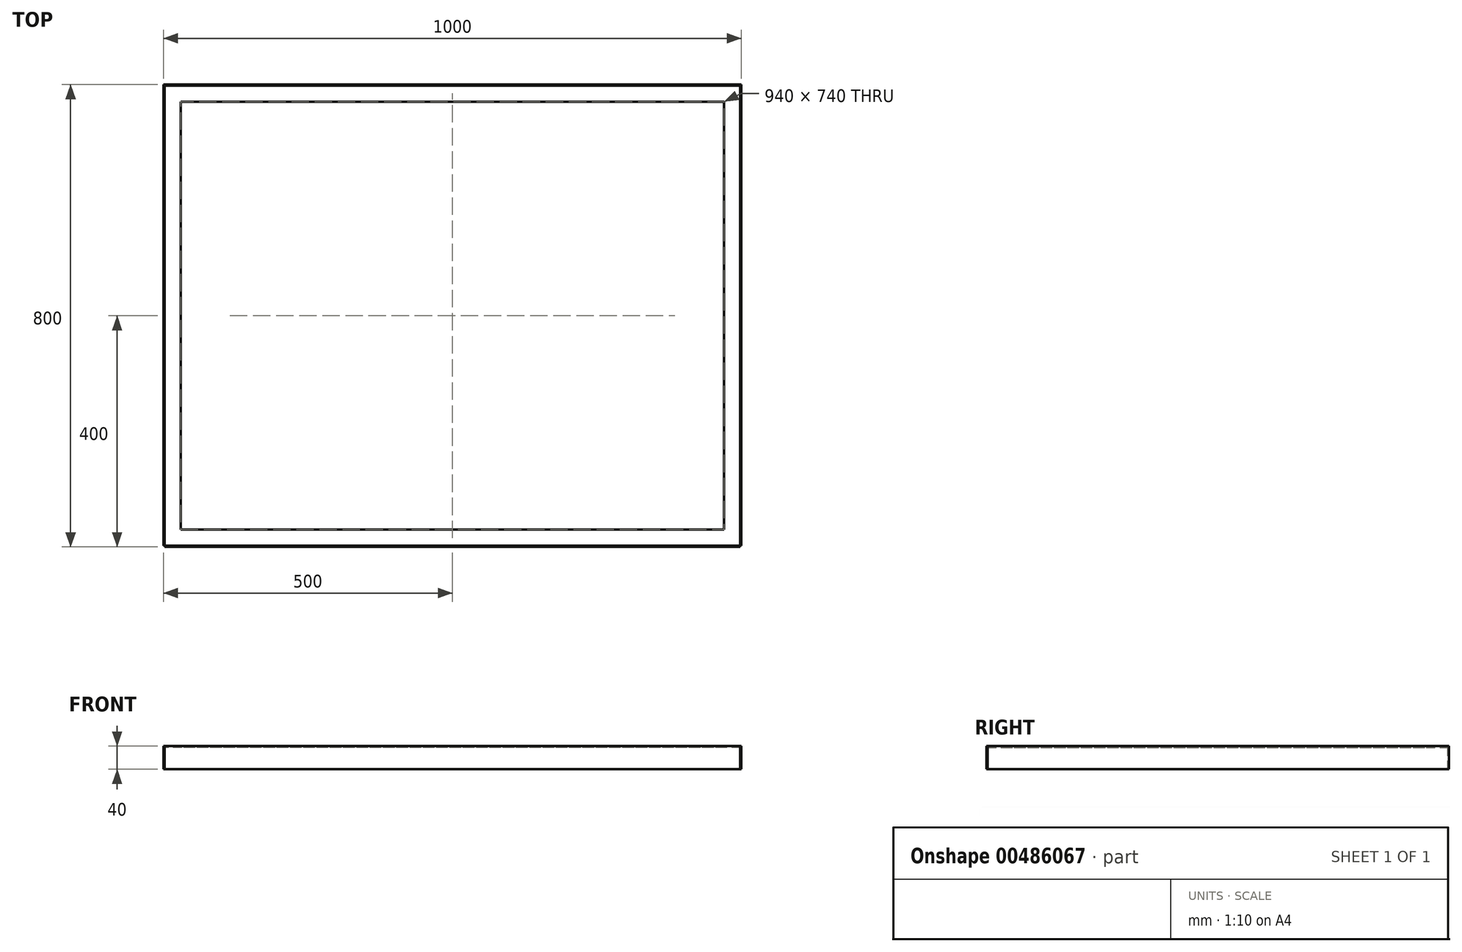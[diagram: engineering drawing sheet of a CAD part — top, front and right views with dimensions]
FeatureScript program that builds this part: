
annotation { "Feature Type Name" : "Feature", "Feature Type Description" : "" }
export const myFeature = defineFeature(function(context is Context, id is Id, definition is map)
    precondition{}
    {
        {
            var Q0;
            Q0=qCreatedBy(makeId("Top.planeOp"),FACE);
            var sketch = newSketch(context, id + "F0", { "sketchPlane" : qUnion([Q0])});
            skLineSegment(sketch, "E0.bottom", {"start": v(119.7, 99.7) * mm, "end": v(1119.7, 99.7) * mm});
            skLineSegment(sketch, "E0.left", {"start": v(119.7, 99.7) * mm, "end": v(119.7, 179.7) * mm});
            skLineSegment(sketch, "E0.right", {"start": v(1119.7, 99.7) * mm, "end": v(1119.7, 179.7) * mm});
            skLineSegment(sketch, "E1.bottom", {"start": v(1119.7, 99.7) * mm, "end": v(119.7, 99.7) * mm});
            skLineSegment(sketch, "E1.top", {"start": v(1119.7, 899.7) * mm, "end": v(119.7, 899.7) * mm});
            skLineSegment(sketch, "E1.left", {"start": v(1119.7, 99.7) * mm, "end": v(1119.7, 899.7) * mm});
            skLineSegment(sketch, "E1.right", {"start": v(119.7, 99.7) * mm, "end": v(119.7, 899.7) * mm});
            skLineSegment(sketch, "E2.0", {"start": v(121.7, 99.7) * mm, "end": v(121.7, 897.7) * mm});
            skLineSegment(sketch, "E2.1", {"start": v(1117.7, 897.7) * mm, "end": v(121.7, 897.7) * mm});
            skLineSegment(sketch, "E2.2", {"start": v(1117.7, 99.7) * mm, "end": v(1117.7, 897.7) * mm});
            skLineSegment(sketch, "E3.0", {"start": v(1119.7, 101.7) * mm, "end": v(119.7, 101.7) * mm});
            skLineSegment(sketch, "E4.0", {"start": v(1119.7, 869.7) * mm, "end": v(1117.7, 869.7) * mm});
            skLineSegment(sketch, "E5.0", {"start": v(1089.7, 99.7) * mm, "end": v(1089.7, 101.7) * mm});
            skLineSegment(sketch, "E6.0", {"start": v(1119.7, 129.7) * mm, "end": v(1117.7, 129.7) * mm});
            skLineSegment(sketch, "E7.0", {"start": v(149.7, 99.7) * mm, "end": v(149.7, 101.7) * mm});
            skLineSegment(sketch, "E8.trimOffspring", {"start": v(121.7, 869.7) * mm, "end": v(119.7, 869.7) * mm});
            skLineSegment(sketch, "E9.trimOffspring", {"start": v(149.7, 897.7) * mm, "end": v(149.7, 899.7) * mm});
            skLineSegment(sketch, "E10.trimOffspring", {"start": v(149.7, 129.7) * mm, "end": v(149.7, 869.7) * mm});
            skLineSegment(sketch, "E11.trimOffspring", {"start": v(121.7, 129.7) * mm, "end": v(119.7, 129.7) * mm});
            skLineSegment(sketch, "E12.trimOffspring", {"start": v(1089.7, 129.7) * mm, "end": v(149.7, 129.7) * mm});
            skLineSegment(sketch, "E13.trimOffspring", {"start": v(1089.7, 129.7) * mm, "end": v(1089.7, 869.7) * mm});
            skLineSegment(sketch, "E14.trimOffspring", {"start": v(1089.7, 869.7) * mm, "end": v(149.7, 869.7) * mm});
            skLineSegment(sketch, "E15.trimOffspring", {"start": v(1089.7, 897.7) * mm, "end": v(1089.7, 899.7) * mm});
            skSolve(sketch);
        }
        {
            var Q0;
            {var subQ3=sQuery(id+"F0.wireOp",EDGE,"E8.trimOffspring");Q0=makeQuery(id+"F0.imprint","IMPRINT",FACE,{"disambiguationData":[TD([[makeQuery(id+"F0.imprint","IMPRINT",EDGE,{"derivedFrom":subQ3}),-1.0]])]});}
            var Q1;
            {var subQ0=sQuery(id+"F0.wireOp",EDGE,"E9.trimOffspring");Q1=makeQuery(id+"F0.imprint","IMPRINT",FACE,{"disambiguationData":[TD([[makeQuery(id+"F0.imprint","IMPRINT",EDGE,{"derivedFrom":subQ0}),-1.0]])]});}
            var Q2;
            {var subQ0=sQuery(id+"F0.wireOp",EDGE,"E8.trimOffspring");Q2=makeQuery(id+"F0.imprint","IMPRINT",FACE,{"disambiguationData":[TD([[makeQuery(id+"F0.imprint","IMPRINT",EDGE,{"derivedFrom":subQ0}),1.0]])]});}
            var Q3;
            {var subQ3=sQuery(id+"F0.wireOp",EDGE,"E4.0");Q3=makeQuery(id+"F0.imprint","IMPRINT",FACE,{"disambiguationData":[TD([[makeQuery(id+"F0.imprint","IMPRINT",EDGE,{"derivedFrom":subQ3}),-1.0]])]});}
            var Q4;
            {var subQ0=sQuery(id+"F0.wireOp",EDGE,"E4.0");Q4=makeQuery(id+"F0.imprint","IMPRINT",FACE,{"disambiguationData":[TD([[makeQuery(id+"F0.imprint","IMPRINT",EDGE,{"derivedFrom":subQ0}),1.0]])]});}
            var Q5;
            {var subQ3=sQuery(id+"F0.wireOp",EDGE,"E6.0");Q5=makeQuery(id+"F0.imprint","IMPRINT",FACE,{"disambiguationData":[TD([[makeQuery(id+"F0.imprint","IMPRINT",EDGE,{"derivedFrom":subQ3}),1.0]])]});}
            var Q6;
            {var subQ0=sQuery(id+"F0.wireOp",EDGE,"E1.left");var subQ1=sQuery(id+"F0.wireOp",EDGE,"E1.bottom");var subQ2=makeQuery(id+"F0.imprint","INTERSECT",VERTEX,{"derivedFrom":[subQ1,subQ0]});Q6=makeQuery(id+"F0.imprint","IMPRINT",FACE,{"disambiguationData":[TD([[makeQuery(id+"F0.imprint","IMPRINT",EDGE,{"disambiguationData":[TD([[subQ2,-1.0]])],"derivedFrom":subQ1}),-1.0]])]});}
            var Q7;
            {var subQ3=sQuery(id+"F0.wireOp",EDGE,"E5.0");Q7=makeQuery(id+"F0.imprint","IMPRINT",FACE,{"disambiguationData":[TD([[makeQuery(id+"F0.imprint","IMPRINT",EDGE,{"derivedFrom":subQ3}),-1.0]])]});}
            var Q8;
            {var subQ0=sQuery(id+"F0.wireOp",EDGE,"E5.0");Q8=makeQuery(id+"F0.imprint","IMPRINT",FACE,{"disambiguationData":[TD([[makeQuery(id+"F0.imprint","IMPRINT",EDGE,{"derivedFrom":subQ0}),1.0]])]});}
            var Q9;
            {var subQ3=sQuery(id+"F0.wireOp",EDGE,"E7.0");Q9=makeQuery(id+"F0.imprint","IMPRINT",FACE,{"disambiguationData":[TD([[makeQuery(id+"F0.imprint","IMPRINT",EDGE,{"derivedFrom":subQ3}),1.0]])]});}
            var Q10;
            {var subQ0=sQuery(id+"F0.wireOp",EDGE,"E1.right");var subQ1=sQuery(id+"F0.wireOp",EDGE,"E1.bottom");var subQ2=makeQuery(id+"F0.imprint","INTERSECT",VERTEX,{"derivedFrom":[subQ1,subQ0]});Q10=makeQuery(id+"F0.imprint","IMPRINT",FACE,{"disambiguationData":[TD([[makeQuery(id+"F0.imprint","IMPRINT",EDGE,{"disambiguationData":[TD([[subQ2,1.0]])],"derivedFrom":subQ1}),-1.0]])]});}
            var Q11;
            {var subQ3=sQuery(id+"F0.wireOp",EDGE,"E11.trimOffspring");Q11=makeQuery(id+"F0.imprint","IMPRINT",FACE,{"disambiguationData":[TD([[makeQuery(id+"F0.imprint","IMPRINT",EDGE,{"derivedFrom":subQ3}),1.0]])]});}
            extrude(context, id + "F1", {"entities" : qUnion([Q0, Q1, Q2, Q3, Q4, Q5, Q6, Q7, Q8, Q9, Q10, Q11]), "oppositeDirection" : true, "depth" : 40 * mm, "offsetDistance" : 25 * mm});
        }
        {
            var Q0;
            Q0=makeQuery(id+"F0.imprint","IMPRINT",FACE,{"disambiguationData":[TD([[makeQuery(id+"F0.imprint","IMPRINT",EDGE,{"derivedFrom":sQuery(id+"F0.wireOp",EDGE,"E10.trimOffspring")}),1.0]])]});
            extrude(context, id + "F2", {"entities" : qUnion([Q0]), "oppositeDirection" : true, "depth" : 2 * mm, "offsetDistance" : 25 * mm});
        }
    });
